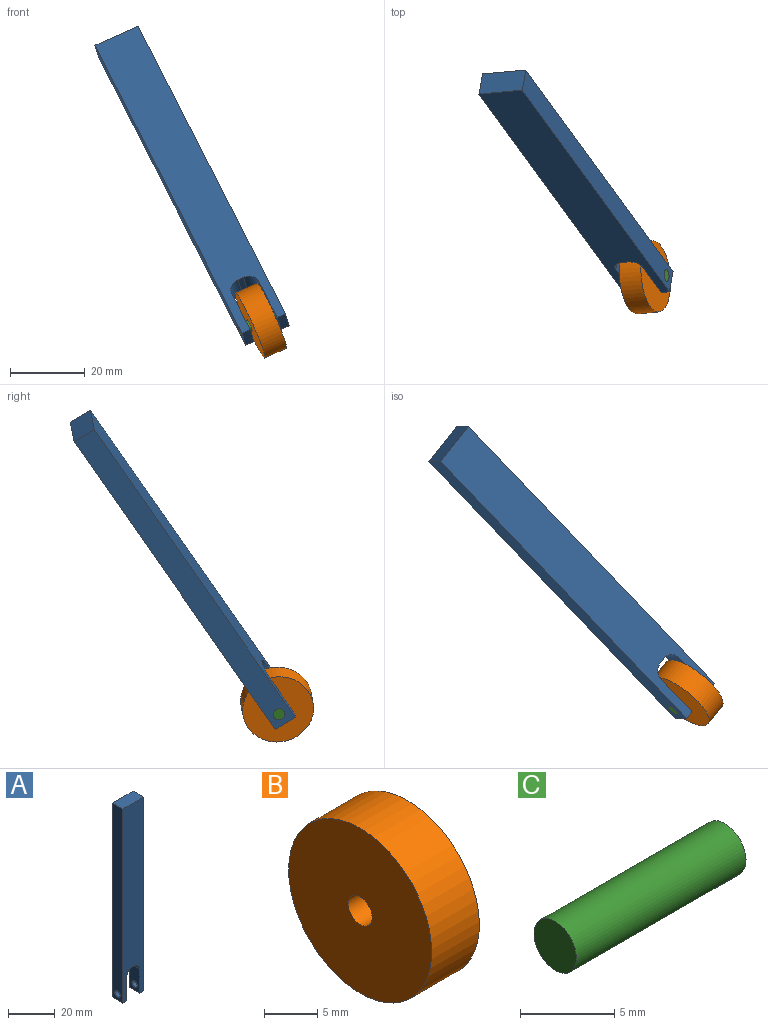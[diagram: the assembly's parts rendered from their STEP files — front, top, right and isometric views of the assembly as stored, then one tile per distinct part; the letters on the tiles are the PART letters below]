
ASSEMBLY  parts=3 mates=2
PART A: 14 faces, bbox 12.7x6.4x101.6 mm
  f0: plane 6.35x1.59mm, normal (0,0,-1), area 10.1mm2, adj f1,f9,f10,f11
  f1: cylinder r=3.17mm len=6.35mm, axis (0,-1,0), area 31.7mm2, adj f0,f2,f10,f11
  f2: plane 12.7x6.35mm, normal (-1,0,0), area 72.7mm2, adj f1,f3,f10,f11,f13
  f3: plane 6.35x2.38mm, normal (0,0,-1), area 15.1mm2, adj f2,f4,f10,f11
  f4: plane 101.6x6.35mm, normal (1,0,0), area 637.2mm2, adj f3,f5,f10,f11,f13
  f5: plane 12.7x6.35mm, normal (0,0,1), area 80.6mm2, adj f4,f6,f10,f11
  f6: plane 101.6x6.35mm, normal (-1,0,0), area 637.2mm2, adj f5,f7,f10,f11,f12
  f7: plane 6.35x2.38mm, normal (0,0,-1), area 15.1mm2, adj f6,f8,f10,f11
  f8: plane 12.7x6.35mm, normal (1,0,0), area 72.7mm2, adj f7,f9,f10,f11,f12
  f9: cylinder r=3.17mm len=6.35mm, axis (0,-1,0), area 31.7mm2, adj f0,f8,f10,f11
  f10: plane 101.6x12.7mm, normal (0,-1,0), area 1168.6mm2, adj f0,f1,f2,f3,f4,f5,f6,f7
  f11: plane 101.6x12.7mm, normal (0,1,0), area 1168.6mm2, adj f0,f1,f2,f3,f4,f5,f6,f7
  f12: cylinder r=1.59mm len=3.18mm, axis (1,0,0), area 23.8mm2, adj f6,f8
  f13: cylinder r=1.59mm len=3.18mm, axis (1,0,0), area 23.8mm2, adj f2,f4
PART B: 4 faces, bbox 6.4x19.1x19.1 mm
  f0: cylinder r=1.59mm len=6.35mm, axis (1,0,0), area 63.3mm2, adj f2,f3
  f1: cylinder r=9.53mm len=19.05mm, axis (1,0,0), area 380mm2, adj f2,f3
  f2: plane 19.05x19.05mm, normal (1,0,0), area 277.1mm2, adj f0,f1
  f3: plane 19.05x19.05mm, normal (-1,0,0), area 277.1mm2, adj f0,f1
PART C: 3 faces, bbox 12.7x3.2x3.2 mm
  f0: cylinder r=1.59mm len=12.7mm, axis (1,0,0), area 126.7mm2, adj f1,f2
  f1: plane 3.18x3.18mm, normal (1,0,0), area 7.9mm2, adj f0
  f2: plane 3.18x3.18mm, normal (-1,0,0), area 7.9mm2, adj f0
PLACE A rot(axis=(-0.79,-0.61,-0.06),41deg) t=(-47.6,-10.64,52.21)mm
PLACE B rot(axis=(-0.9,-0.41,-0.12),59.6deg) t=(-43.58,2.45,40.66)mm
PLACE C rot(axis=(-0.9,-0.41,-0.12),59.6deg) t=(-43.58,2.45,40.66)mm
MATE fastened B.f0 <-> C.f0  axis (0.91,0.08,0.41) through (-26.31,-35.55,17.51)mm
MATE revolute B.f0 <-> A.f12  axis (0.91,0.08,0.41) through (-26.31,-35.55,17.51)mm
